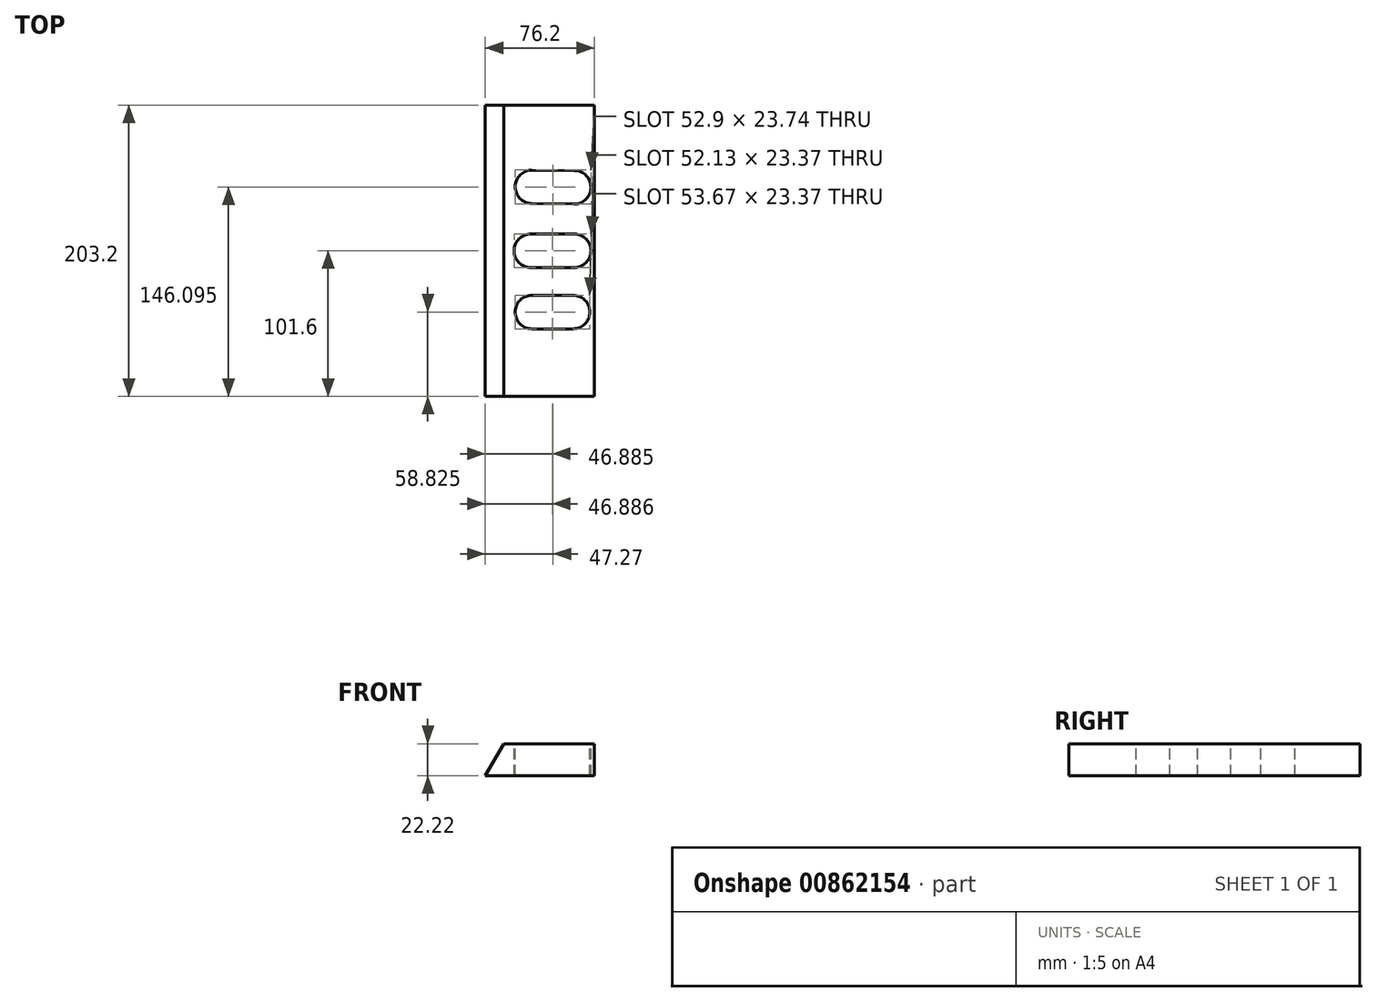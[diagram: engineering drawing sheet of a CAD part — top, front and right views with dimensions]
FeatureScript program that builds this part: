
annotation { "Feature Type Name" : "Feature", "Feature Type Description" : "" }
export const myFeature = defineFeature(function(context is Context, id is Id, definition is map)
    precondition{}
    {
        {
            var Q0;
            Q0=qCreatedBy(makeId("Front.planeOp"),FACE);
            var sketch = newSketch(context, id + "F0", { "sketchPlane" : qUnion([Q0])});
            skLineSegment(sketch, "E0", {"start": v(-66.83, -27.34) * mm, "end": v(9.37, -27.34) * mm});
            skLineSegment(sketch, "E1", {"start": v(9.37, -27.34) * mm, "end": v(9.37, -5.12) * mm});
            skLineSegment(sketch, "E2", {"start": v(9.37, -5.12) * mm, "end": v(-54, -5.12) * mm});
            skLineSegment(sketch, "E3", {"start": v(-54, -5.12) * mm, "end": v(-66.83, -27.34) * mm});
            skSolve(sketch);
        }
        {
            var Q0;
            Q0=makeQuery(id+"F0.imprint","IMPRINT",FACE,{"disambiguationData":[TD([[makeQuery(id+"F0.imprint","IMPRINT",EDGE,{"derivedFrom":sQuery(id+"F0.wireOp",EDGE,"E0")}),1.0]])]});
            extrude(context, id + "F1", {"entities" : qUnion([Q0]), "endBound" : BoundingType.SYMMETRIC, "depth" : 203.2 * mm, "offsetDistance" : 25.4 * mm});
        }
        {
            var Q0;
            Q0=makeQuery(id+"F1.opExtrude","SWEPT_FACE",FACE,{"disambiguationData":[OSD([sQuery(id+"F0.wireOp",EDGE,"E2")])]});
            var sketch = newSketch(context, id + "F2", { "sketchPlane" : qUnion([Q0])});
            skArc(sketch, "E4", {"start": v(-4.94, 32.63) * mm, "mid": v(6.89, 44.16) * mm, "end": v(-4.65, 56) * mm});
            skArc(sketch, "E5", {"start": v(-34.18, 56.36) * mm, "mid": v(-46, 44.83) * mm, "end": v(-34.47, 33) * mm});
            skArc(sketch, "E6", {"start": v(-35.1, 11.68) * mm, "mid": v(-46.78, 0) * mm, "end": v(-35.1, -11.68) * mm});
            skArc(sketch, "E7", {"start": v(-34.33, -31.1) * mm, "mid": v(-46, -42.78) * mm, "end": v(-34.33, -54.46) * mm});
            skArc(sketch, "E8", {"start": v(-4.8, -11.68) * mm, "mid": v(6.89, 0) * mm, "end": v(-4.8, 11.68) * mm});
            skArc(sketch, "E9", {"start": v(-5.56, -54.46) * mm, "mid": v(6.12, -42.78) * mm, "end": v(-5.56, -31.1) * mm});
            skLineSegment(sketch, "E10", {"start": v(-4.65, 56) * mm, "end": v(-34.18, 56.36) * mm});
            skLineSegment(sketch, "E11", {"start": v(-4.94, 32.63) * mm, "end": v(-34.47, 33) * mm});
            skLineSegment(sketch, "E12", {"start": v(-4.8, -11.68) * mm, "end": v(-35.1, -11.68) * mm});
            skLineSegment(sketch, "E13", {"start": v(-5.56, -31.1) * mm, "end": v(-34.33, -31.1) * mm});
            skLineSegment(sketch, "E14", {"start": v(-5.56, -54.46) * mm, "end": v(-34.33, -54.46) * mm});
            skLineSegment(sketch, "E15.MirrorCS", {"start": v(-4.8, 11.68) * mm, "end": v(-35.1, 11.68) * mm});
            skSolve(sketch);
        }
        {
            var Q0;
            Q0=makeQuery(id+"F2.imprint","IMPRINT",FACE,{"disambiguationData":[TD([[makeQuery(id+"F2.imprint","IMPRINT",EDGE,{"derivedFrom":sQuery(id+"F2.wireOp",EDGE,"E4")}),1.0]])]});
            var Q1;
            Q1=makeQuery(id+"F2.imprint","IMPRINT",FACE,{"disambiguationData":[TD([[makeQuery(id+"F2.imprint","IMPRINT",EDGE,{"derivedFrom":sQuery(id+"F2.wireOp",EDGE,"E6")}),1.0]])]});
            var Q2;
            Q2=makeQuery(id+"F2.imprint","IMPRINT",FACE,{"disambiguationData":[TD([[makeQuery(id+"F2.imprint","IMPRINT",EDGE,{"derivedFrom":sQuery(id+"F2.wireOp",EDGE,"E7")}),1.0]])]});
            extrude(context, id + "F3", {"entities" : qUnion([Q0, Q1, Q2]), "operationType" : NewBodyOperationType.REMOVE, "oppositeDirection" : true, "depth" : 25.4 * mm, "offsetDistance" : 25.4 * mm});
        }
    });
